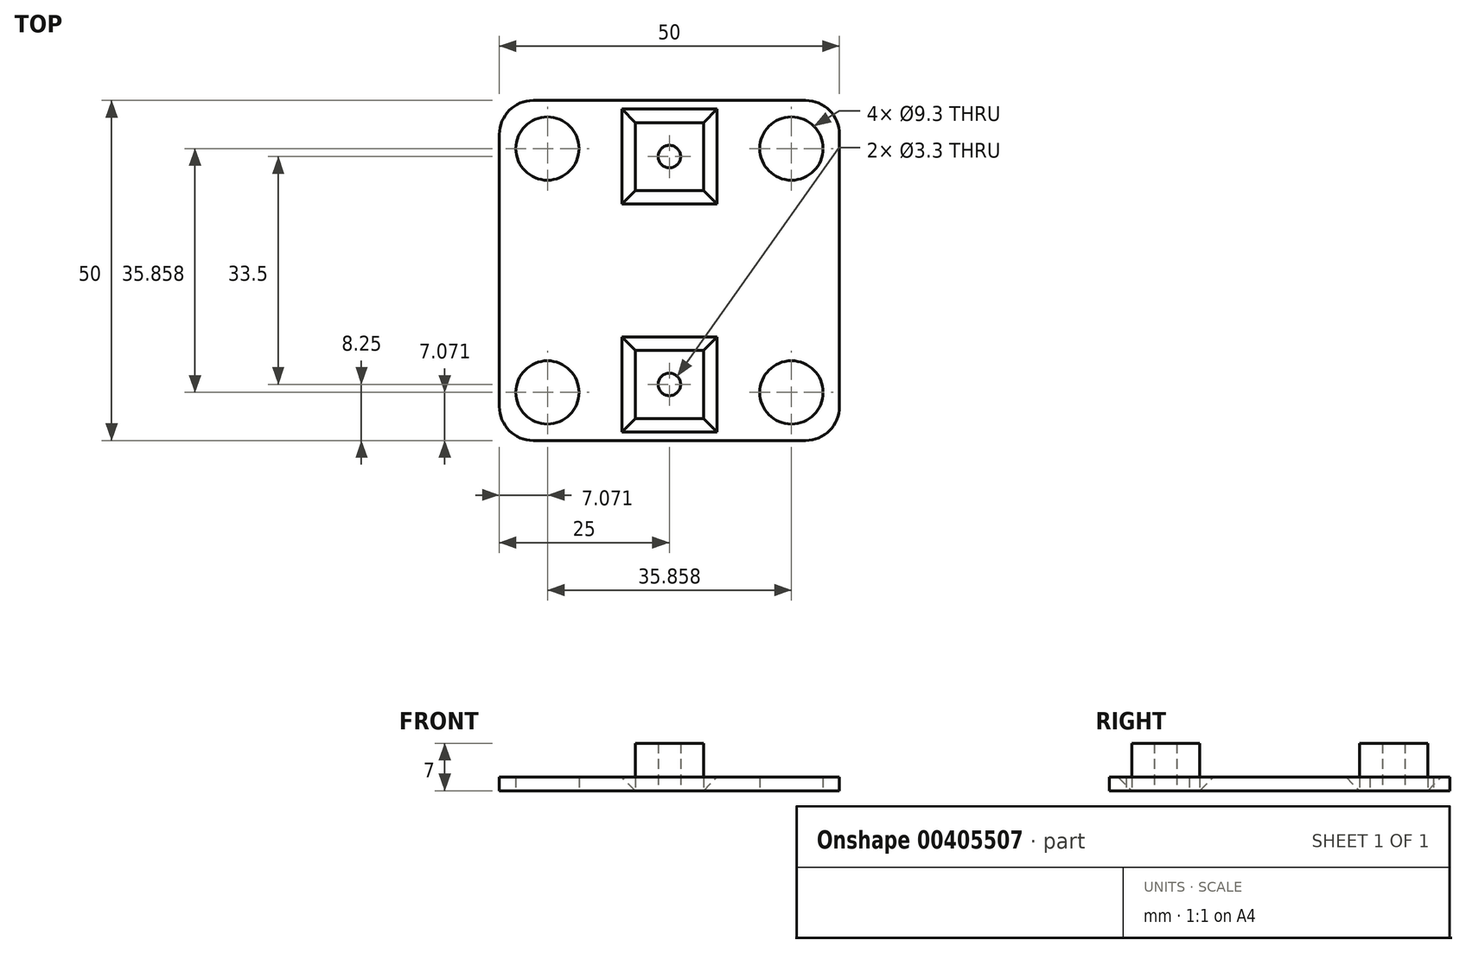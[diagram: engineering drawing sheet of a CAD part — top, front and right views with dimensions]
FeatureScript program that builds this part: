
annotation { "Feature Type Name" : "Feature", "Feature Type Description" : "" }
export const myFeature = defineFeature(function(context is Context, id is Id, definition is map)
    precondition{}
    {
        {
            var Q0;
            Q0=qCreatedBy(makeId("Top.planeOp"),FACE);
            var sketch = newSketch(context, id + "F0", { "sketchPlane" : qUnion([Q0])});
            skLineSegment(sketch, "E0.bottom", {"start": v(5, 0) * mm, "end": v(45, 0) * mm});
            skLineSegment(sketch, "E0.top", {"start": v(5, -50) * mm, "end": v(45, -50) * mm});
            skLineSegment(sketch, "E0.left", {"start": v(0, -5) * mm, "end": v(0, -45) * mm});
            skLineSegment(sketch, "E0.right", {"start": v(50, -5) * mm, "end": v(50, -45) * mm});
            skLineSegment(sketch, "E1", {"start": v(25, 0) * mm, "end": v(25, -50) * mm, "construction": true});
            skLineSegment(sketch, "E2", {"start": v(0, -25) * mm, "end": v(50, -25) * mm, "construction": true});
            skLineSegment(sketch, "E3", {"start": v(25, -25) * mm, "end": v(25, -8.25) * mm, "construction": true});
            skLineSegment(sketch, "E4", {"start": v(25, -25) * mm, "end": v(25, -41.75) * mm, "construction": true});
            skCircle(sketch, "E5", {"center": v(25, -8.25) * mm, "radius": 1.65 * mm});
            skCircle(sketch, "E6", {"center": v(25, -41.75) * mm, "radius": 1.65 * mm});
            skLineSegment(sketch, "E7", {"start": v(20, -50) * mm, "end": v(20, 0) * mm, "construction": true});
            skLineSegment(sketch, "E8", {"start": v(30, 0) * mm, "end": v(30, -50) * mm, "construction": true});
            skLineSegment(sketch, "E9", {"start": v(0, -36.75) * mm, "end": v(50, -36.75) * mm, "construction": true});
            skLineSegment(sketch, "E10", {"start": v(0, -46.75) * mm, "end": v(50, -46.75) * mm, "construction": true});
            skLineSegment(sketch, "E11", {"start": v(0, -3.25) * mm, "end": v(50, -3.25) * mm, "construction": true});
            skLineSegment(sketch, "E12", {"start": v(0, -13.25) * mm, "end": v(50, -13.25) * mm, "construction": true});
            skLineSegment(sketch, "E13", {"start": v(50, -8.25) * mm, "end": v(0, -8.25) * mm, "construction": true});
            skLineSegment(sketch, "E14", {"start": v(50, -41.75) * mm, "end": v(0, -41.75) * mm, "construction": true});
            skLineSegment(sketch, "E15", {"start": v(20, -3.25) * mm, "end": v(20, -13.25) * mm});
            skLineSegment(sketch, "E16", {"start": v(20, -13.25) * mm, "end": v(30, -13.25) * mm});
            skLineSegment(sketch, "E17", {"start": v(30, -13.25) * mm, "end": v(30, -3.25) * mm});
            skLineSegment(sketch, "E18", {"start": v(30, -3.25) * mm, "end": v(20, -3.25) * mm});
            skLineSegment(sketch, "E19", {"start": v(20, -36.75) * mm, "end": v(20, -46.75) * mm});
            skLineSegment(sketch, "E20", {"start": v(20, -46.75) * mm, "end": v(30, -46.75) * mm});
            skLineSegment(sketch, "E21", {"start": v(30, -46.75) * mm, "end": v(30, -36.75) * mm});
            skLineSegment(sketch, "E22", {"start": v(30, -36.75) * mm, "end": v(20, -36.75) * mm});
            skLineSegment(sketch, "E23", {"start": v(0, 0) * mm, "end": v(50, -50) * mm, "construction": true});
            skLineSegment(sketch, "E24", {"start": v(50, 0) * mm, "end": v(0, -50) * mm, "construction": true});
            skLineSegment(sketch, "E25.bottom", {"start": v(7.07, -7.07) * mm, "end": v(42.93, -7.07) * mm, "construction": true});
            skLineSegment(sketch, "E25.top", {"start": v(7.07, -42.93) * mm, "end": v(42.93, -42.93) * mm, "construction": true});
            skLineSegment(sketch, "E25.left", {"start": v(7.07, -7.07) * mm, "end": v(7.07, -42.93) * mm, "construction": true});
            skLineSegment(sketch, "E25.right", {"start": v(42.93, -7.07) * mm, "end": v(42.93, -42.93) * mm, "construction": true});
            skCircle(sketch, "E26", {"center": v(7.07, -7.07) * mm, "radius": 4.65 * mm});
            skCircle(sketch, "E27", {"center": v(42.93, -7.07) * mm, "radius": 4.65 * mm});
            skCircle(sketch, "E28", {"center": v(42.93, -42.93) * mm, "radius": 4.65 * mm});
            skCircle(sketch, "E29", {"center": v(7.07, -42.93) * mm, "radius": 4.65 * mm});
            skPoint(sketch, "E30.visualSharp", {"position": v(0, -50) * mm});
            skArc(sketch, "E30.filletArc", {"start": v(0, -45) * mm, "mid": v(1.46, -48.54) * mm, "end": v(5, -50) * mm});
            skPoint(sketch, "E31.visualSharp", {"position": v(0, 0) * mm});
            skArc(sketch, "E31.filletArc", {"start": v(5, 0) * mm, "mid": v(1.46, -1.46) * mm, "end": v(0, -5) * mm});
            skPoint(sketch, "E32.visualSharp", {"position": v(50, 0) * mm});
            skArc(sketch, "E32.filletArc", {"start": v(50, -5) * mm, "mid": v(48.54, -1.46) * mm, "end": v(45, 0) * mm});
            skPoint(sketch, "E33.visualSharp", {"position": v(50, -50) * mm});
            skArc(sketch, "E33.filletArc", {"start": v(45, -50) * mm, "mid": v(48.54, -48.54) * mm, "end": v(50, -45) * mm});
            skSolve(sketch);
        }
        {
            var Q0;
            Q0=makeQuery(id+"F0.imprint","IMPRINT",FACE,{"disambiguationData":[TD([[makeQuery(id+"F0.imprint","IMPRINT",EDGE,{"derivedFrom":sQuery(id+"F0.wireOp",EDGE,"E6")}),-1.0]])]});
            var Q1;
            Q1=makeQuery(id+"F0.imprint","IMPRINT",FACE,{"disambiguationData":[TD([[makeQuery(id+"F0.imprint","IMPRINT",EDGE,{"derivedFrom":sQuery(id+"F0.wireOp",EDGE,"E5")}),-1.0]])]});
            extrude(context, id + "F1", {"entities" : qUnion([Q0, Q1]), "depth" : 7 * mm});
        }
        {
            var Q0;
            Q0=makeQuery(id+"F0.imprint","IMPRINT",FACE,{"disambiguationData":[TD([[makeQuery(id+"F0.imprint","IMPRINT",EDGE,{"derivedFrom":sQuery(id+"F0.wireOp",EDGE,"E0.bottom")}),-1.0]])]});
            extrude(context, id + "F2", {"entities" : qUnion([Q0]), "depth" : 2 * mm});
        }
        {
            var Q0;
            Q0=makeQuery(id+"F2.opExtrude","CAP_EDGE",EDGE,{"disambiguationData":[OSD([sQuery(id+"F0.wireOp",EDGE,"E20")])],"isStart":false});
            var Q1;
            Q1=makeQuery(id+"F2.opExtrude","CAP_EDGE",EDGE,{"disambiguationData":[OSD([sQuery(id+"F0.wireOp",EDGE,"E17")])],"isStart":false});
            var Q2;
            Q2=makeQuery(id+"F2.opExtrude","CAP_EDGE",EDGE,{"disambiguationData":[OSD([sQuery(id+"F0.wireOp",EDGE,"E21")])],"isStart":false});
            var Q3;
            Q3=makeQuery(id+"F2.opExtrude","CAP_EDGE",EDGE,{"disambiguationData":[OSD([sQuery(id+"F0.wireOp",EDGE,"E16")])],"isStart":false});
            var Q4;
            Q4=makeQuery(id+"F2.opExtrude","CAP_EDGE",EDGE,{"disambiguationData":[OSD([sQuery(id+"F0.wireOp",EDGE,"E18")])],"isStart":false});
            var Q5;
            Q5=makeQuery(id+"F2.opExtrude","CAP_EDGE",EDGE,{"disambiguationData":[OSD([sQuery(id+"F0.wireOp",EDGE,"E22")])],"isStart":false});
            var Q6;
            Q6=makeQuery(id+"F2.opExtrude","CAP_EDGE",EDGE,{"disambiguationData":[OSD([sQuery(id+"F0.wireOp",EDGE,"E15")])],"isStart":false});
            var Q7;
            Q7=makeQuery(id+"F2.opExtrude","CAP_EDGE",EDGE,{"disambiguationData":[OSD([sQuery(id+"F0.wireOp",EDGE,"E19")])],"isStart":false});
            chamfer(context, id + "F3", {"entities" : qUnion([Q0, Q1, Q2, Q3, Q4, Q5, Q6, Q7]), "width" : 2 * mm, "tangentPropagation" : true});
        }
    });
